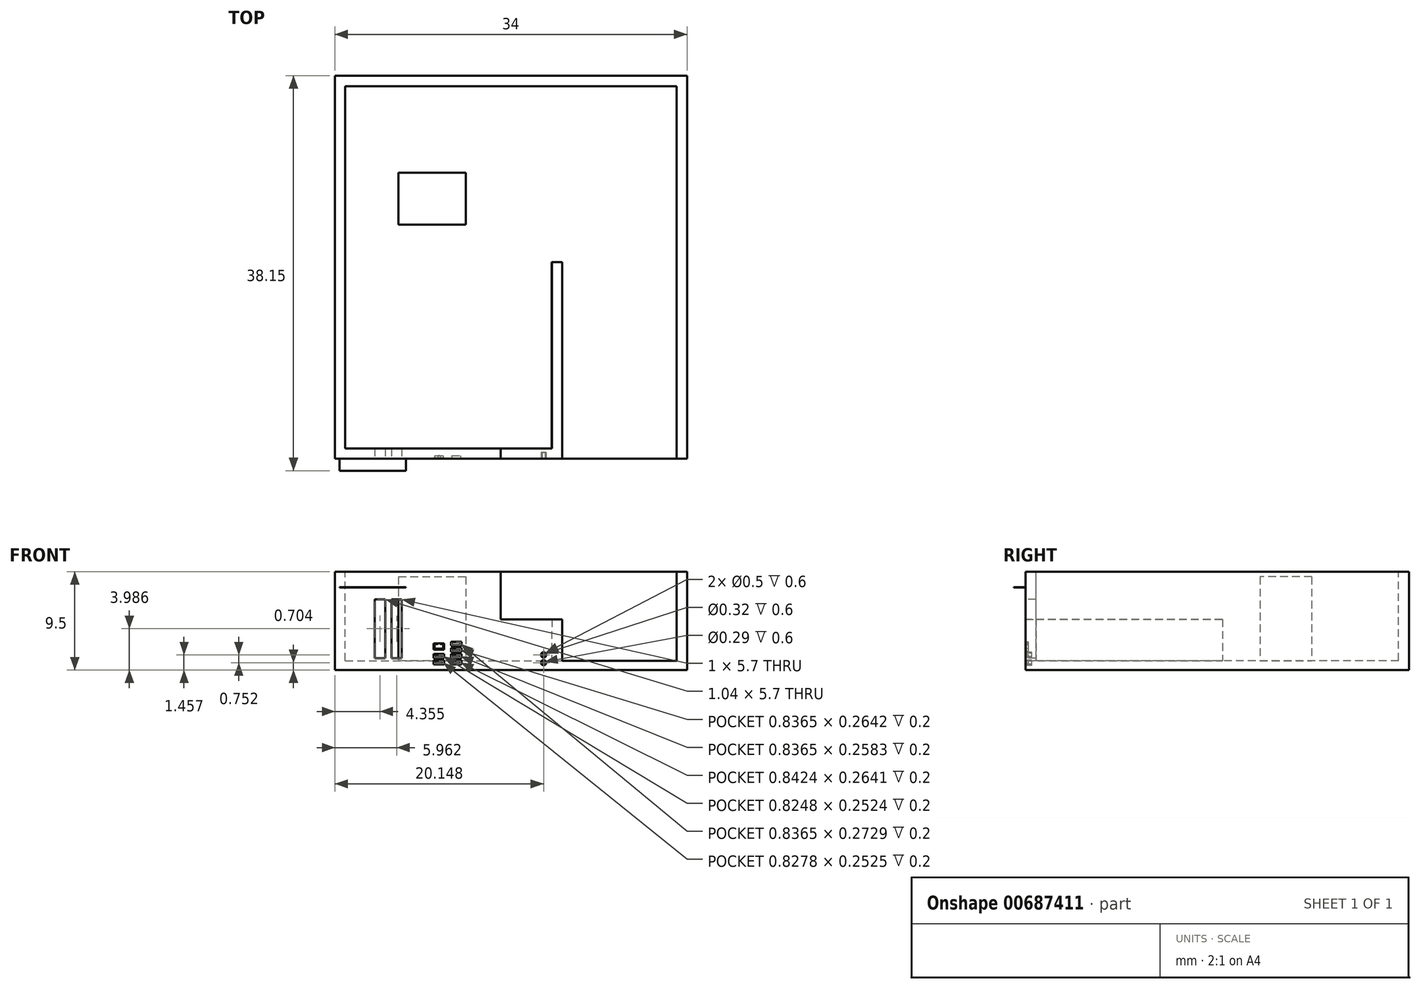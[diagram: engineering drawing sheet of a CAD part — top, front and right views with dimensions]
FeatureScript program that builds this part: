
annotation { "Feature Type Name" : "Feature", "Feature Type Description" : "" }
export const myFeature = defineFeature(function(context is Context, id is Id, definition is map)
    precondition{}
    {
        {
            var Q0;
            Q0=qCreatedBy(makeId("Top.planeOp"),FACE);
            var sketch = newSketch(context, id + "F0", { "sketchPlane" : qUnion([Q0])});
            skLineSegment(sketch, "E0.bottom", {"start": v(0, 0) * mm, "end": v(-34, 0) * mm});
            skLineSegment(sketch, "E0.top", {"start": v(0, 37) * mm, "end": v(-34, 37) * mm});
            skLineSegment(sketch, "E0.left", {"start": v(0, 0) * mm, "end": v(0, 37) * mm});
            skLineSegment(sketch, "E0.right", {"start": v(-34, 0) * mm, "end": v(-34, 37) * mm});
            skSolve(sketch);
        }
        {
            var Q0;
            Q0 = qSketchRegion(id + "F0", true);
            extrude(context, id + "F1", {"entities" : qUnion([Q0]), "depth" : 9.5 * mm, "offsetDistance" : 25 * mm});
        }
        {
            var Q0;
            Q0=makeQuery(id+"F1.opExtrude","CAP_FACE",FACE,{"disambiguationData":[OSD([sQuery(id+"F0.wireOp",EDGE,"E0.bottom"),sQuery(id+"F0.wireOp",EDGE,"E0.top"),sQuery(id+"F0.wireOp",EDGE,"E0.left"),sQuery(id+"F0.wireOp",EDGE,"E0.right")])],"isStart":false});
            var sketch = newSketch(context, id + "F2", { "sketchPlane" : qUnion([Q0])});
            skLineSegment(sketch, "E1", {"start": v(-33, 36) * mm, "end": v(-33, 1) * mm});
            skLineSegment(sketch, "E2", {"start": v(-33, 36) * mm, "end": v(-1, 36) * mm});
            skLineSegment(sketch, "E3", {"start": v(0, 37) * mm, "end": v(-1, 37) * mm});
            skLineSegment(sketch, "E4", {"start": v(-1, 36) * mm, "end": v(-1, 0) * mm});
            skLineSegment(sketch, "E5", {"start": v(-33, 1) * mm, "end": v(-18, 1) * mm});
            skLineSegment(sketch, "E6", {"start": v(-18, 1) * mm, "end": v(-18, 0) * mm});
            skPoint(sketch, "E7.start.orphan", {"position": v(-33, 0) * mm});
            skPoint(sketch, "E8.end.orphan", {"position": v(-33, 37) * mm});
            skPoint(sketch, "E9.orphan", {"position": v(0, 36) * mm});
            skLineSegment(sketch, "E10", {"start": v(-1, 0) * mm, "end": v(0, 0) * mm});
            skLineSegment(sketch, "E11", {"start": v(0, 0) * mm, "end": v(0, 37) * mm});
            skLineSegment(sketch, "E12", {"start": v(0, 37) * mm, "end": v(-34, 37) * mm});
            skLineSegment(sketch, "E13", {"start": v(-34, 37) * mm, "end": v(-34, 0) * mm});
            skLineSegment(sketch, "E14", {"start": v(-34, 0) * mm, "end": v(-18, 0) * mm});
            skSolve(sketch);
        }
        {
            var Q0;
            Q0=makeQuery(id+"F2.imprint","IMPRINT",FACE,{"disambiguationData":[TD([[makeQuery(id+"F2.imprint","IMPRINT",EDGE,{"derivedFrom":sQuery(id+"F2.wireOp",EDGE,"E1")}),1.0]])]});
            extrude(context, id + "F3", {"entities" : qUnion([Q0]), "operationType" : NewBodyOperationType.REMOVE, "oppositeDirection" : true, "depth" : 8.6 * mm, "offsetDistance" : 25 * mm});
        }
        {
            var Q0;
            Q0=makeQuery(id+"F3.boolean.opBoolean","COPY",FACE,{"derivedFrom":makeQuery(id+"F3.opExtrude","CAP_FACE",FACE,{"disambiguationData":[OSD([sQuery(id+"F0.wireOp",EDGE,"E0.bottom"),sQuery(id+"F2.wireOp",EDGE,"E1"),sQuery(id+"F2.wireOp",EDGE,"E2"),sQuery(id+"F2.wireOp",EDGE,"E4"),sQuery(id+"F2.wireOp",EDGE,"E5"),sQuery(id+"F2.wireOp",EDGE,"E6")])],"isStart":false})});
            cPlane(context, id + "F4", {"entities" : qUnion([Q0]), "cplaneType" : CPlaneType.OFFSET, "offset" : 4 * mm, "width" : 150 * mm, "height" : 150 * mm});
        }
        {
            var Q0;
            Q0=qCreatedBy(id+"F4.planeOp",FACE);
            var sketch = newSketch(context, id + "F5", { "sketchPlane" : qUnion([Q0])});
            skLineSegment(sketch, "E15.bottom", {"start": v(-18.05, 1) * mm, "end": v(-13.05, 1) * mm});
            skLineSegment(sketch, "E15.top", {"start": v(-18.05, 0) * mm, "end": v(-12.05, 0) * mm});
            skLineSegment(sketch, "E15.left", {"start": v(-18.05, 1) * mm, "end": v(-18.05, 0) * mm});
            skLineSegment(sketch, "E16.top", {"start": v(-12.05, 19) * mm, "end": v(-13.05, 19) * mm});
            skLineSegment(sketch, "E16.right", {"start": v(-13.05, 1) * mm, "end": v(-13.05, 19) * mm});
            skLineSegment(sketch, "E17", {"start": v(-12.05, 19) * mm, "end": v(-12.05, 0) * mm});
            skSolve(sketch);
        }
        {
            var Q0;
            Q0=qCreatedBy(makeId("Top.planeOp"),FACE);
            var sketch = newSketch(context, id + "F6", { "sketchPlane" : qUnion([Q0])});
            skLineSegment(sketch, "E18.bottom", {"start": v(-18.02, 0) * mm, "end": v(-12.07, 0) * mm});
            skLineSegment(sketch, "E18.top", {"start": v(-18.02, 1) * mm, "end": v(-13.07, 1) * mm});
            skLineSegment(sketch, "E18.left", {"start": v(-18.02, 0) * mm, "end": v(-18.02, 1) * mm});
            skLineSegment(sketch, "E19.bottom", {"start": v(-13.07, 0) * mm, "end": v(-12.07, 0) * mm});
            skLineSegment(sketch, "E19.top", {"start": v(-13.07, 19) * mm, "end": v(-12.07, 19) * mm});
            skLineSegment(sketch, "E19.left", {"start": v(-13.07, 1) * mm, "end": v(-13.07, 19) * mm});
            skLineSegment(sketch, "E19.right", {"start": v(-12.07, 0) * mm, "end": v(-12.07, 19) * mm});
            skPoint(sketch, "E20.orphan", {"position": v(-12.02, 0) * mm});
            skSolve(sketch);
        }
        {
            var Q1;
            Q1=makeQuery(id+"F5.imprint","IMPRINT",FACE,{"disambiguationData":[TD([[makeQuery(id+"F5.imprint","IMPRINT",EDGE,{"derivedFrom":sQuery(id+"F5.wireOp",EDGE,"E15.bottom")}),-1.0]])]});
            var Q2;
            Q2=makeQuery(id+"F6.imprint","IMPRINT",FACE,{"disambiguationData":[TD([[makeQuery(id+"F6.imprint","IMPRINT",EDGE,{"derivedFrom":sQuery(id+"F6.wireOp",EDGE,"E18.bottom")}),1.0]])]});
            loft(context, id + "F7", {"operationType" : NewBodyOperationType.ADD, "sheetProfilesArray" : [{ "sheetProfileEntities" : qUnion([Q1]) }, { "sheetProfileEntities" : qUnion([Q2]) }]});
        }
        {
            var Q0;
            Q0=qCreatedBy(makeId("Top.planeOp"),FACE);
            var sketch = newSketch(context, id + "F8", { "sketchPlane" : qUnion([Q0])});
            skLineSegment(sketch, "E21.bottom", {"start": v(-27.86, 27.62) * mm, "end": v(-21.36, 27.62) * mm});
            skLineSegment(sketch, "E21.top", {"start": v(-27.86, 22.62) * mm, "end": v(-21.36, 22.62) * mm});
            skLineSegment(sketch, "E21.left", {"start": v(-27.86, 27.62) * mm, "end": v(-27.86, 22.62) * mm});
            skLineSegment(sketch, "E21.right", {"start": v(-21.36, 27.62) * mm, "end": v(-21.36, 22.62) * mm});
            skSolve(sketch);
        }
        {
            var Q0;
            Q0 = qSketchRegion(id + "F8", true);
            extrude(context, id + "F9", {"entities" : qUnion([Q0]), "operationType" : NewBodyOperationType.ADD, "depth" : 9 * mm, "offsetDistance" : 25 * mm});
        }
        {
            var Q0;
            Q0=makeQuery(id+"F7.boolean.opBoolean","MERGE",FACE,{"derivedFrom":[makeQuery(id+"F1.opExtrude","SWEPT_FACE",FACE,{"disambiguationData":[OSD([sQuery(id+"F0.wireOp",EDGE,"E0.bottom")])]}),makeQuery(id+"F7.opLoft","SWEPT_FACE",FACE,{"disambiguationData":[OSD([sQuery(id+"F5.wireOp",EDGE,"E15.top"),sQuery(id+"F5.wireOp",EDGE,"E15.left"),sQuery(id+"F5.wireOp",EDGE,"E17"),sQuery(id+"F6.wireOp",EDGE,"E18.bottom"),sQuery(id+"F6.wireOp",EDGE,"E18.left"),sQuery(id+"F6.wireOp",EDGE,"E19.bottom")])]})]});
            var sketch = newSketch(context, id + "F10", { "sketchPlane" : qUnion([Q0])});
            skLineSegment(sketch, "E22.bottom", {"start": v(-29.13, 1.14) * mm, "end": v(-30.16, 1.14) * mm});
            skLineSegment(sketch, "E22.top", {"start": v(-29.13, 6.83) * mm, "end": v(-30.16, 6.83) * mm});
            skLineSegment(sketch, "E22.left", {"start": v(-29.13, 1.14) * mm, "end": v(-29.13, 6.83) * mm});
            skLineSegment(sketch, "E22.right", {"start": v(-30.16, 1.14) * mm, "end": v(-30.16, 6.83) * mm});
            skLineSegment(sketch, "E23.bottom", {"start": v(-28.54, 1.14) * mm, "end": v(-27.54, 1.14) * mm});
            skLineSegment(sketch, "E23.top", {"start": v(-28.54, 6.83) * mm, "end": v(-27.54, 6.83) * mm});
            skLineSegment(sketch, "E23.left", {"start": v(-28.54, 1.14) * mm, "end": v(-28.54, 6.83) * mm});
            skLineSegment(sketch, "E23.right", {"start": v(-27.54, 1.14) * mm, "end": v(-27.54, 6.83) * mm});
            skSolve(sketch);
        }
        {
            var Q0;
            Q0=makeQuery(id+"F10.imprint","IMPRINT",FACE,{"disambiguationData":[TD([[makeQuery(id+"F10.imprint","IMPRINT",EDGE,{"derivedFrom":sQuery(id+"F10.wireOp",EDGE,"E22.bottom")}),-1.0]])]});
            var Q1;
            Q1=makeQuery(id+"F10.imprint","IMPRINT",FACE,{"disambiguationData":[TD([[makeQuery(id+"F10.imprint","IMPRINT",EDGE,{"derivedFrom":sQuery(id+"F10.wireOp",EDGE,"E23.bottom")}),1.0]])]});
            extrude(context, id + "F11", {"entities" : qUnion([Q0, Q1]), "operationType" : NewBodyOperationType.REMOVE, "oppositeDirection" : true, "depth" : 6 * mm, "offsetDistance" : 25 * mm});
        }
        {
            var Q0;
            Q0=makeQuery(id+"F7.boolean.opBoolean","MERGE",FACE,{"derivedFrom":[makeQuery(id+"F1.opExtrude","SWEPT_FACE",FACE,{"disambiguationData":[OSD([sQuery(id+"F0.wireOp",EDGE,"E0.bottom")])]}),makeQuery(id+"F7.opLoft","SWEPT_FACE",FACE,{"disambiguationData":[OSD([sQuery(id+"F5.wireOp",EDGE,"E15.top"),sQuery(id+"F5.wireOp",EDGE,"E15.left"),sQuery(id+"F5.wireOp",EDGE,"E17"),sQuery(id+"F6.wireOp",EDGE,"E18.bottom"),sQuery(id+"F6.wireOp",EDGE,"E18.left"),sQuery(id+"F6.wireOp",EDGE,"E19.bottom")])]})]});
            var sketch = newSketch(context, id + "F12", { "sketchPlane" : qUnion([Q0])});
            skLineSegment(sketch, "E24.bottom", {"start": v(-33.55, 8) * mm, "end": v(-27.13, 8) * mm});
            skLineSegment(sketch, "E24.top", {"start": v(-33.55, 7.97) * mm, "end": v(-27.13, 7.97) * mm});
            skLineSegment(sketch, "E24.left", {"start": v(-33.55, 8) * mm, "end": v(-33.55, 7.97) * mm});
            skLineSegment(sketch, "E24.right", {"start": v(-27.13, 8) * mm, "end": v(-27.13, 7.97) * mm});
            skSolve(sketch);
        }
        {
            var Q0;
            Q0 = qSketchRegion(id + "F12", true);
            extrude(context, id + "F13", {"entities" : qUnion([Q0]), "operationType" : NewBodyOperationType.ADD, "depth" : 1.15 * mm, "offsetDistance" : 25 * mm});
        }
        {
            var Q0;
            Q0=makeQuery(id+"F7.boolean.opBoolean","MERGE",FACE,{"derivedFrom":[makeQuery(id+"F1.opExtrude","SWEPT_FACE",FACE,{"disambiguationData":[OSD([sQuery(id+"F0.wireOp",EDGE,"E0.bottom")])]}),makeQuery(id+"F7.opLoft","SWEPT_FACE",FACE,{"disambiguationData":[OSD([sQuery(id+"F5.wireOp",EDGE,"E15.top"),sQuery(id+"F5.wireOp",EDGE,"E15.left"),sQuery(id+"F5.wireOp",EDGE,"E17"),sQuery(id+"F6.wireOp",EDGE,"E18.bottom"),sQuery(id+"F6.wireOp",EDGE,"E18.left"),sQuery(id+"F6.wireOp",EDGE,"E19.bottom")])]})]});
            var sketch = newSketch(context, id + "F14", { "sketchPlane" : qUnion([Q0])});
            skLineSegment(sketch, "E25.bottom", {"start": v(-24.46, 1.14) * mm, "end": v(-23.46, 1.14) * mm});
            skLineSegment(sketch, "E25.top", {"start": v(-24.46, 1.54) * mm, "end": v(-23.46, 1.54) * mm});
            skLineSegment(sketch, "E25.left", {"start": v(-24.46, 1.14) * mm, "end": v(-24.46, 1.54) * mm});
            skLineSegment(sketch, "E25.right", {"start": v(-23.46, 1.14) * mm, "end": v(-23.46, 1.54) * mm});
            skLineSegment(sketch, "E26.bottom", {"start": v(-24.46, 0.94) * mm, "end": v(-23.46, 0.94) * mm});
            skLineSegment(sketch, "E26.top", {"start": v(-24.46, 0.54) * mm, "end": v(-23.46, 0.54) * mm});
            skLineSegment(sketch, "E26.left", {"start": v(-24.46, 0.94) * mm, "end": v(-24.46, 0.54) * mm});
            skLineSegment(sketch, "E26.right", {"start": v(-23.46, 0.94) * mm, "end": v(-23.46, 0.54) * mm});
            skLineSegment(sketch, "E27.bottom", {"start": v(-23.46, 1.98) * mm, "end": v(-24.46, 1.98) * mm});
            skLineSegment(sketch, "E27.top", {"start": v(-23.46, 2.58) * mm, "end": v(-24.46, 2.58) * mm});
            skLineSegment(sketch, "E27.left", {"start": v(-23.46, 1.98) * mm, "end": v(-23.46, 2.58) * mm});
            skLineSegment(sketch, "E27.right", {"start": v(-24.46, 1.98) * mm, "end": v(-24.46, 2.58) * mm});
            skLineSegment(sketch, "E28.bottom", {"start": v(-22.8, 0.94) * mm, "end": v(-21.8, 0.94) * mm});
            skLineSegment(sketch, "E28.top", {"start": v(-22.8, 0.54) * mm, "end": v(-21.8, 0.54) * mm});
            skLineSegment(sketch, "E28.left", {"start": v(-22.8, 0.94) * mm, "end": v(-22.8, 0.54) * mm});
            skLineSegment(sketch, "E28.right", {"start": v(-21.8, 0.94) * mm, "end": v(-21.8, 0.54) * mm});
            skLineSegment(sketch, "E29", {"start": v(-22.8, 0.54) * mm, "end": v(-22.8, 0.94) * mm});
            skPoint(sketch, "E30.left.start.orphan", {"position": v(-22.75, 1.96) * mm});
            skPoint(sketch, "E31.left.start.orphan", {"position": v(-22.75, 1.54) * mm});
            skLineSegment(sketch, "E32.bottom", {"start": v(-22.8, 1.14) * mm, "end": v(-21.8, 1.14) * mm});
            skLineSegment(sketch, "E32.top", {"start": v(-22.8, 1.54) * mm, "end": v(-21.8, 1.54) * mm});
            skLineSegment(sketch, "E32.left", {"start": v(-22.8, 1.14) * mm, "end": v(-22.8, 1.54) * mm});
            skLineSegment(sketch, "E32.right", {"start": v(-21.8, 1.14) * mm, "end": v(-21.8, 1.54) * mm});
            skLineSegment(sketch, "E33.bottom", {"start": v(-22.8, 1.74) * mm, "end": v(-21.8, 1.74) * mm});
            skLineSegment(sketch, "E33.top", {"start": v(-22.8, 2.14) * mm, "end": v(-21.8, 2.14) * mm});
            skLineSegment(sketch, "E33.left", {"start": v(-22.8, 1.74) * mm, "end": v(-22.8, 2.14) * mm});
            skLineSegment(sketch, "E33.right", {"start": v(-21.8, 1.74) * mm, "end": v(-21.8, 2.14) * mm});
            skLineSegment(sketch, "E34.bottom", {"start": v(-22.8, 2.34) * mm, "end": v(-21.8, 2.34) * mm});
            skLineSegment(sketch, "E34.top", {"start": v(-22.8, 2.74) * mm, "end": v(-21.8, 2.74) * mm});
            skLineSegment(sketch, "E34.left", {"start": v(-22.8, 2.34) * mm, "end": v(-22.8, 2.74) * mm});
            skLineSegment(sketch, "E34.right", {"start": v(-21.8, 2.34) * mm, "end": v(-21.8, 2.74) * mm});
            skSolve(sketch);
        }
        {
            var Q0;
            Q0=makeQuery(id+"F14.imprint","IMPRINT",FACE,{"disambiguationData":[TD([[makeQuery(id+"F14.imprint","IMPRINT",EDGE,{"derivedFrom":sQuery(id+"F14.wireOp",EDGE,"E27.bottom")}),-1.0]])]});
            var Q1;
            Q1=makeQuery(id+"F14.imprint","IMPRINT",FACE,{"disambiguationData":[TD([[makeQuery(id+"F14.imprint","IMPRINT",EDGE,{"derivedFrom":sQuery(id+"F14.wireOp",EDGE,"E25.bottom")}),1.0]])]});
            var Q2;
            Q2=makeQuery(id+"F14.imprint","IMPRINT",FACE,{"disambiguationData":[TD([[makeQuery(id+"F14.imprint","IMPRINT",EDGE,{"derivedFrom":sQuery(id+"F14.wireOp",EDGE,"E28.bottom")}),-1.0]])]});
            var Q3;
            Q3=makeQuery(id+"F14.imprint","IMPRINT",FACE,{"disambiguationData":[TD([[makeQuery(id+"F14.imprint","IMPRINT",EDGE,{"derivedFrom":sQuery(id+"F14.wireOp",EDGE,"E32.bottom")}),1.0]])]});
            var Q4;
            Q4=makeQuery(id+"F14.imprint","IMPRINT",FACE,{"disambiguationData":[TD([[makeQuery(id+"F14.imprint","IMPRINT",EDGE,{"derivedFrom":sQuery(id+"F14.wireOp",EDGE,"E33.bottom")}),1.0]])]});
            var Q5;
            Q5=makeQuery(id+"F14.imprint","IMPRINT",FACE,{"disambiguationData":[TD([[makeQuery(id+"F14.imprint","IMPRINT",EDGE,{"derivedFrom":sQuery(id+"F14.wireOp",EDGE,"E34.bottom")}),1.0]])]});
            var Q6;
            Q6=makeQuery(id+"F14.imprint","IMPRINT",FACE,{"disambiguationData":[TD([[makeQuery(id+"F14.imprint","IMPRINT",EDGE,{"derivedFrom":sQuery(id+"F14.wireOp",EDGE,"E26.bottom")}),-1.0]])]});
            extrude(context, id + "F15", {"entities" : qUnion([Q0, Q1, Q2, Q3, Q4, Q5, Q6]), "operationType" : NewBodyOperationType.REMOVE, "oppositeDirection" : true, "depth" : 0.1 * mm, "offsetDistance" : 25 * mm});
        }
        {
            var Q0;
            Q0=makeQuery(id+"F15.boolean.opBoolean","COPY",FACE,{"derivedFrom":makeQuery(id+"F15.opExtrude","CAP_FACE",FACE,{"disambiguationData":[OSD([sQuery(id+"F14.wireOp",EDGE,"E27.bottom"),sQuery(id+"F14.wireOp",EDGE,"E27.top"),sQuery(id+"F14.wireOp",EDGE,"E27.left"),sQuery(id+"F14.wireOp",EDGE,"E27.right")])],"isStart":false})});
            var sketch = newSketch(context, id + "F16", { "sketchPlane" : qUnion([Q0])});
            skLineSegment(sketch, "E35.bottom", {"start": v(-24.38, 2.05) * mm, "end": v(-23.55, 2.05) * mm});
            skLineSegment(sketch, "E35.top", {"start": v(-24.38, 2.52) * mm, "end": v(-24.06, 2.52) * mm});
            skLineSegment(sketch, "E35.left", {"start": v(-24.38, 2.05) * mm, "end": v(-24.38, 2.52) * mm});
            skLineSegment(sketch, "E35.right", {"start": v(-23.55, 2.05) * mm, "end": v(-23.55, 2.52) * mm});
            skLineSegment(sketch, "E36.top", {"start": v(-24.06, 2.58) * mm, "end": v(-23.85, 2.58) * mm});
            skLineSegment(sketch, "E36.left", {"start": v(-24.06, 2.52) * mm, "end": v(-24.06, 2.58) * mm});
            skLineSegment(sketch, "E36.right", {"start": v(-23.85, 2.52) * mm, "end": v(-23.85, 2.58) * mm});
            skLineSegment(sketch, "E37.trimOffspring", {"start": v(-23.85, 2.52) * mm, "end": v(-23.55, 2.52) * mm});
            skLineSegment(sketch, "E38.bottom", {"start": v(-24.38, 1.21) * mm, "end": v(-23.56, 1.21) * mm});
            skLineSegment(sketch, "E38.top", {"start": v(-24.38, 1.46) * mm, "end": v(-23.56, 1.46) * mm});
            skLineSegment(sketch, "E38.left", {"start": v(-24.38, 1.21) * mm, "end": v(-24.38, 1.46) * mm});
            skLineSegment(sketch, "E38.right", {"start": v(-23.56, 1.21) * mm, "end": v(-23.56, 1.46) * mm});
            skLineSegment(sketch, "E39.bottom", {"start": v(-24.38, 0.6) * mm, "end": v(-23.55, 0.6) * mm});
            skLineSegment(sketch, "E39.top", {"start": v(-24.38, 0.86) * mm, "end": v(-23.55, 0.86) * mm});
            skLineSegment(sketch, "E39.left", {"start": v(-24.38, 0.6) * mm, "end": v(-24.38, 0.86) * mm});
            skLineSegment(sketch, "E39.right", {"start": v(-23.55, 0.6) * mm, "end": v(-23.55, 0.86) * mm});
            skLineSegment(sketch, "E40.bottom", {"start": v(-22.72, 0.6) * mm, "end": v(-21.88, 0.6) * mm});
            skLineSegment(sketch, "E40.top", {"start": v(-22.72, 0.87) * mm, "end": v(-21.88, 0.87) * mm});
            skLineSegment(sketch, "E40.left", {"start": v(-22.72, 0.6) * mm, "end": v(-22.72, 0.87) * mm});
            skLineSegment(sketch, "E40.right", {"start": v(-21.88, 0.6) * mm, "end": v(-21.88, 0.87) * mm});
            skLineSegment(sketch, "E41.bottom", {"start": v(-22.71, 1.2) * mm, "end": v(-21.88, 1.2) * mm});
            skLineSegment(sketch, "E41.top", {"start": v(-22.71, 1.47) * mm, "end": v(-21.88, 1.47) * mm});
            skLineSegment(sketch, "E41.left", {"start": v(-22.71, 1.2) * mm, "end": v(-22.71, 1.47) * mm});
            skLineSegment(sketch, "E41.right", {"start": v(-21.88, 1.2) * mm, "end": v(-21.88, 1.47) * mm});
            skLineSegment(sketch, "E42.bottom", {"start": v(-22.71, 1.8) * mm, "end": v(-21.88, 1.8) * mm});
            skLineSegment(sketch, "E42.top", {"start": v(-22.71, 2.07) * mm, "end": v(-21.88, 2.07) * mm});
            skLineSegment(sketch, "E42.left", {"start": v(-22.71, 1.8) * mm, "end": v(-22.71, 2.07) * mm});
            skLineSegment(sketch, "E42.right", {"start": v(-21.88, 1.8) * mm, "end": v(-21.88, 2.07) * mm});
            skLineSegment(sketch, "E43.bottom", {"start": v(-22.71, 2.41) * mm, "end": v(-21.88, 2.41) * mm});
            skLineSegment(sketch, "E43.top", {"start": v(-22.71, 2.68) * mm, "end": v(-21.88, 2.68) * mm});
            skLineSegment(sketch, "E43.left", {"start": v(-22.71, 2.41) * mm, "end": v(-22.71, 2.68) * mm});
            skLineSegment(sketch, "E43.right", {"start": v(-21.88, 2.41) * mm, "end": v(-21.88, 2.68) * mm});
            skSolve(sketch);
        }
        {
            var Q0;
            Q0=makeQuery(id+"F16.imprint","IMPRINT",FACE,{"disambiguationData":[TD([[makeQuery(id+"F16.imprint","IMPRINT",EDGE,{"derivedFrom":sQuery(id+"F16.wireOp",EDGE,"E35.bottom")}),1.0]])]});
            var Q1;
            Q1=makeQuery(id+"F16.imprint","IMPRINT",FACE,{"disambiguationData":[TD([[makeQuery(id+"F16.imprint","IMPRINT",EDGE,{"derivedFrom":sQuery(id+"F16.wireOp",EDGE,"E38.bottom")}),1.0]])]});
            var Q2;
            Q2=makeQuery(id+"F16.imprint","IMPRINT",FACE,{"disambiguationData":[TD([[makeQuery(id+"F16.imprint","IMPRINT",EDGE,{"derivedFrom":sQuery(id+"F16.wireOp",EDGE,"E39.bottom")}),1.0]])]});
            var Q3;
            Q3=makeQuery(id+"F16.imprint","IMPRINT",FACE,{"disambiguationData":[TD([[makeQuery(id+"F16.imprint","IMPRINT",EDGE,{"derivedFrom":sQuery(id+"F16.wireOp",EDGE,"E40.bottom")}),1.0]])]});
            var Q4;
            Q4=makeQuery(id+"F16.imprint","IMPRINT",FACE,{"disambiguationData":[TD([[makeQuery(id+"F16.imprint","IMPRINT",EDGE,{"derivedFrom":sQuery(id+"F16.wireOp",EDGE,"E41.bottom")}),1.0]])]});
            var Q5;
            Q5=makeQuery(id+"F16.imprint","IMPRINT",FACE,{"disambiguationData":[TD([[makeQuery(id+"F16.imprint","IMPRINT",EDGE,{"derivedFrom":sQuery(id+"F16.wireOp",EDGE,"E42.bottom")}),1.0]])]});
            var Q6;
            Q6=makeQuery(id+"F16.imprint","IMPRINT",FACE,{"disambiguationData":[TD([[makeQuery(id+"F16.imprint","IMPRINT",EDGE,{"derivedFrom":sQuery(id+"F16.wireOp",EDGE,"E43.bottom")}),1.0]])]});
            extrude(context, id + "F17", {"entities" : qUnion([Q0, Q1, Q2, Q3, Q4, Q5, Q6]), "operationType" : NewBodyOperationType.REMOVE, "oppositeDirection" : true, "depth" : 0.2 * mm, "offsetDistance" : 25 * mm});
        }
        {
            var Q0;
            Q0=makeQuery(id+"F7.boolean.opBoolean","MERGE",FACE,{"derivedFrom":[makeQuery(id+"F1.opExtrude","SWEPT_FACE",FACE,{"disambiguationData":[OSD([sQuery(id+"F0.wireOp",EDGE,"E0.bottom")])]}),makeQuery(id+"F7.opLoft","SWEPT_FACE",FACE,{"disambiguationData":[OSD([sQuery(id+"F5.wireOp",EDGE,"E15.top"),sQuery(id+"F5.wireOp",EDGE,"E15.left"),sQuery(id+"F5.wireOp",EDGE,"E17"),sQuery(id+"F6.wireOp",EDGE,"E18.bottom"),sQuery(id+"F6.wireOp",EDGE,"E18.left"),sQuery(id+"F6.wireOp",EDGE,"E19.bottom")])]})]});
            var sketch = newSketch(context, id + "F18", { "sketchPlane" : qUnion([Q0])});
            skCircle(sketch, "E44", {"center": v(-13.85, 0.7) * mm, "radius": 0.25 * mm});
            skCircle(sketch, "E45", {"center": v(-13.85, 1.46) * mm, "radius": 0.25 * mm});
            skPoint(sketch, "E46.trimOffspring.end.orphan", {"position": v(-13.85, 2.2) * mm});
            skCircle(sketch, "E47", {"center": v(-13.85, 1.46) * mm, "radius": 0.22 * mm});
            skCircle(sketch, "E48", {"center": v(-13.85, 1.46) * mm, "radius": 0.16 * mm});
            skCircle(sketch, "E49", {"center": v(-13.85, 0.7) * mm, "radius": 0.22 * mm});
            skCircle(sketch, "E50", {"center": v(-13.85, 0.7) * mm, "radius": 0.15 * mm});
            skSolve(sketch);
        }
        {
            var Q0;
            Q0=makeQuery(id+"F18.imprint","IMPRINT",FACE,{"disambiguationData":[TD([[makeQuery(id+"F18.imprint","IMPRINT",EDGE,{"derivedFrom":sQuery(id+"F18.wireOp",EDGE,"E44")}),1.0]])]});
            var Q1;
            Q1=makeQuery(id+"F18.imprint","IMPRINT",FACE,{"disambiguationData":[TD([[makeQuery(id+"F18.imprint","IMPRINT",EDGE,{"derivedFrom":sQuery(id+"F18.wireOp",EDGE,"E50")}),1.0]])]});
            var Q2;
            Q2=makeQuery(id+"F18.imprint","IMPRINT",FACE,{"disambiguationData":[TD([[makeQuery(id+"F18.imprint","IMPRINT",EDGE,{"derivedFrom":sQuery(id+"F18.wireOp",EDGE,"E48")}),1.0]])]});
            var Q3;
            Q3=makeQuery(id+"F18.imprint","IMPRINT",FACE,{"disambiguationData":[TD([[makeQuery(id+"F18.imprint","IMPRINT",EDGE,{"derivedFrom":sQuery(id+"F18.wireOp",EDGE,"E45")}),1.0]])]});
            extrude(context, id + "F19", {"entities" : qUnion([Q0, Q1, Q2, Q3]), "operationType" : NewBodyOperationType.REMOVE, "oppositeDirection" : true, "depth" : 0.6 * mm, "offsetDistance" : 25 * mm});
        }
    });
